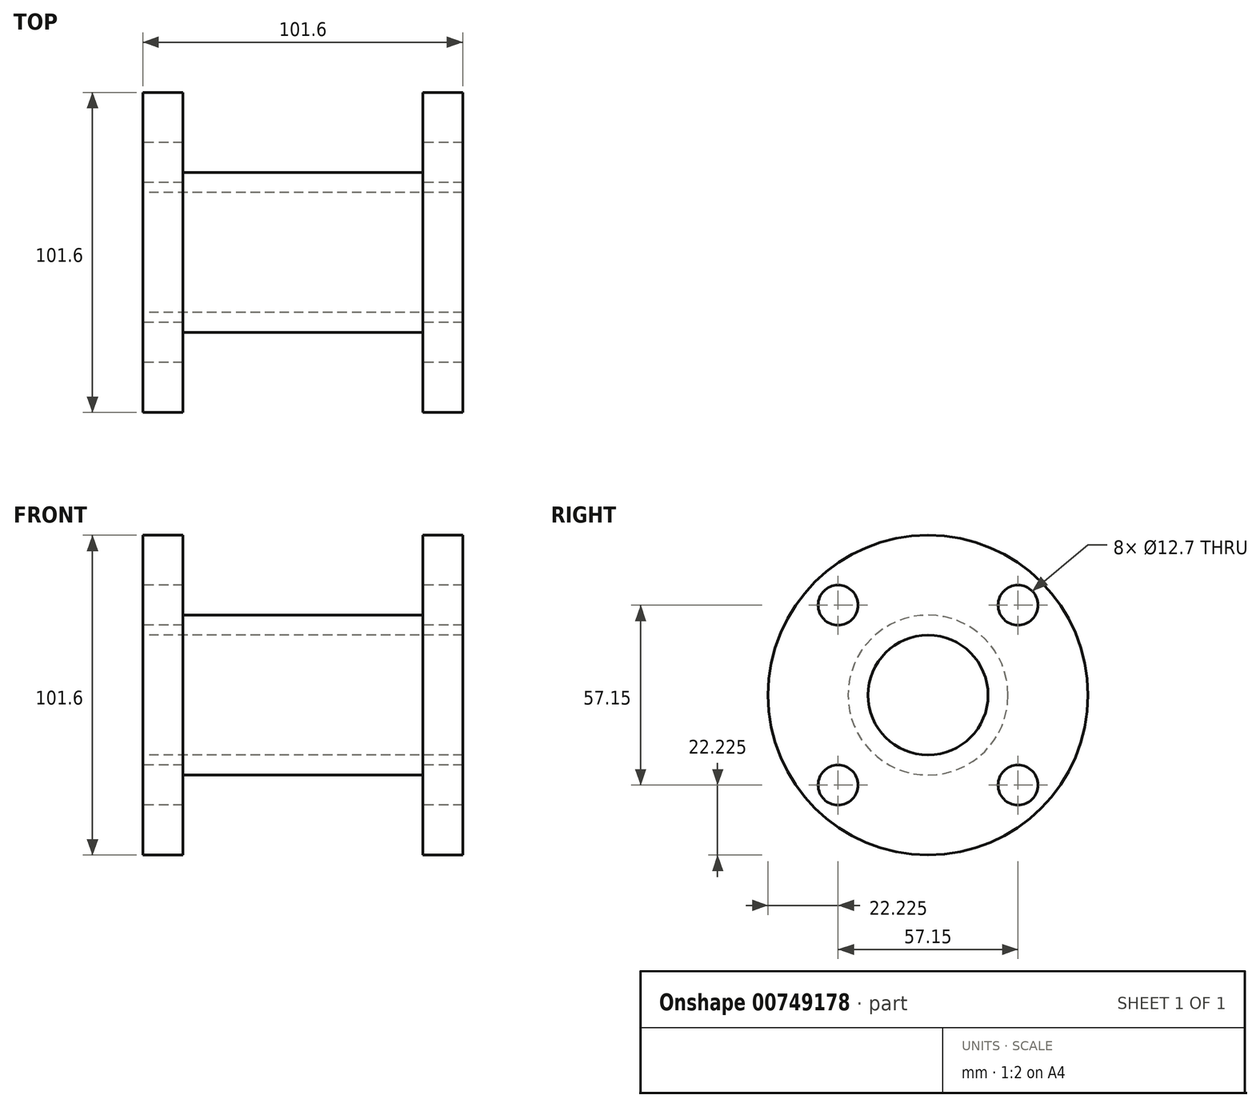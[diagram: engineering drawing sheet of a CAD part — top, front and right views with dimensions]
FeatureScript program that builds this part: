
annotation { "Feature Type Name" : "Feature", "Feature Type Description" : "" }
export const myFeature = defineFeature(function(context is Context, id is Id, definition is map)
    precondition{}
    {
        {
            var Q0;
            Q0=qCreatedBy(makeId("Top.planeOp"),FACE);
            var sketch = newSketch(context, id + "F0", { "sketchPlane" : qUnion([Q0])});
            skLineSegment(sketch, "E0", {"start": v(101.6, -50.8) * mm, "end": v(101.6, -19.05) * mm});
            skLineSegment(sketch, "E1", {"start": v(101.6, -19.05) * mm, "end": v(0, -19.05) * mm});
            skLineSegment(sketch, "E2", {"start": v(0, -19.05) * mm, "end": v(0, -50.8) * mm});
            skLineSegment(sketch, "E3", {"start": v(0, -50.8) * mm, "end": v(101.6, -50.8) * mm});
            skLineSegment(sketch, "E4", {"start": v(0, -25.4) * mm, "end": v(101.6, -25.4) * mm});
            skLineSegment(sketch, "E5", {"start": v(12.7, -19.05) * mm, "end": v(12.7, -50.8) * mm});
            skLineSegment(sketch, "E6", {"start": v(88.9, -19.05) * mm, "end": v(88.9, -50.8) * mm});
            skLineSegment(sketch, "E7", {"start": v(0, 0) * mm, "end": v(101.6, 0) * mm});
            skSolve(sketch);
        }
        {
            var Q0;
            {var subQ0=sQuery(id+"F0.wireOp",EDGE,"E2");var subQ1=sQuery(id+"F0.wireOp",EDGE,"E1");var subQ2=makeQuery(id+"F0.imprint","INTERSECT",VERTEX,{"derivedFrom":[subQ1,subQ0]});Q0=makeQuery(id+"F0.imprint","IMPRINT",FACE,{"disambiguationData":[TD([[makeQuery(id+"F0.imprint","IMPRINT",EDGE,{"disambiguationData":[TD([[subQ2,1.0]])],"derivedFrom":subQ1}),1.0]])]});}
            var Q1;
            {var subQ0=sQuery(id+"F0.wireOp",EDGE,"E3");var subQ1=sQuery(id+"F0.wireOp",EDGE,"E2");var subQ2=makeQuery(id+"F0.imprint","INTERSECT",VERTEX,{"derivedFrom":[subQ1,subQ0]});Q1=makeQuery(id+"F0.imprint","IMPRINT",FACE,{"disambiguationData":[TD([[makeQuery(id+"F0.imprint","IMPRINT",EDGE,{"disambiguationData":[TD([[subQ2,1.0]])],"derivedFrom":subQ1}),1.0]])]});}
            var Q2;
            {var subQ0=sQuery(id+"F0.wireOp",EDGE,"E5");var subQ1=sQuery(id+"F0.wireOp",EDGE,"E1");var subQ2=makeQuery(id+"F0.imprint","INTERSECT",VERTEX,{"derivedFrom":[subQ1,subQ0]});Q2=makeQuery(id+"F0.imprint","IMPRINT",FACE,{"disambiguationData":[TD([[makeQuery(id+"F0.imprint","IMPRINT",EDGE,{"disambiguationData":[TD([[subQ2,1.0]])],"derivedFrom":subQ1}),1.0]])]});}
            var Q3;
            {var subQ0=sQuery(id+"F0.wireOp",EDGE,"E1");var subQ1=sQuery(id+"F0.wireOp",EDGE,"E0");var subQ2=makeQuery(id+"F0.imprint","INTERSECT",VERTEX,{"derivedFrom":[subQ1,subQ0]});Q3=makeQuery(id+"F0.imprint","IMPRINT",FACE,{"disambiguationData":[TD([[makeQuery(id+"F0.imprint","IMPRINT",EDGE,{"disambiguationData":[TD([[subQ2,1.0]])],"derivedFrom":subQ1}),1.0]])]});}
            var Q4;
            {var subQ0=sQuery(id+"F0.wireOp",EDGE,"E3");var subQ1=sQuery(id+"F0.wireOp",EDGE,"E0");var subQ2=makeQuery(id+"F0.imprint","INTERSECT",VERTEX,{"derivedFrom":[subQ1,subQ0]});Q4=makeQuery(id+"F0.imprint","IMPRINT",FACE,{"disambiguationData":[TD([[makeQuery(id+"F0.imprint","IMPRINT",EDGE,{"disambiguationData":[TD([[subQ2,-1.0]])],"derivedFrom":subQ1}),1.0]])]});}
            var Q5;
            Q5=sQuery(id+"F0.wireOp",EDGE,"E7");
            revolve(context, id + "F1", {"surfaceOperationType" : NewSurfaceOperationType.NEW, "entities" : qUnion([Q0, Q1, Q2, Q3, Q4]), "axis" : qUnion([Q5]), "revolveType" : RevolveType.FULL});
        }
        {
            var Q0;
            Q0=makeQuery(id+"F1.opRevolve","SWEPT_FACE",FACE,{"disambiguationData":[OSD([sQuery(id+"F0.wireOp",EDGE,"E2")])]});
            var sketch = newSketch(context, id + "F2", { "sketchPlane" : qUnion([Q0])});
            skCircle(sketch, "E8", {"center": v(-28.58, 28.58) * mm, "radius": 6.35 * mm});
            skCircle(sketch, "E9", {"center": v(28.58, 28.58) * mm, "radius": 6.35 * mm});
            skCircle(sketch, "E10", {"center": v(28.58, -28.58) * mm, "radius": 6.35 * mm});
            skCircle(sketch, "E11", {"center": v(-28.58, -28.58) * mm, "radius": 6.35 * mm});
            skCircle(sketch, "E12.0", {"center": v(0, 0) * mm, "radius": 19.05 * mm});
            skCircle(sketch, "E13.0", {"center": v(0, 0) * mm, "radius": 50.8 * mm});
            skSolve(sketch);
        }
        {
            var Q0;
            Q0=makeQuery(id+"F2.imprint","IMPRINT",FACE,{"disambiguationData":[TD([[makeQuery(id+"F2.imprint","IMPRINT",EDGE,{"derivedFrom":sQuery(id+"F2.wireOp",EDGE,"E8")}),1.0]])]});
            var Q1;
            Q1=makeQuery(id+"F2.imprint","IMPRINT",FACE,{"disambiguationData":[TD([[makeQuery(id+"F2.imprint","IMPRINT",EDGE,{"derivedFrom":sQuery(id+"F2.wireOp",EDGE,"E9")}),1.0]])]});
            var Q2;
            Q2=makeQuery(id+"F2.imprint","IMPRINT",FACE,{"disambiguationData":[TD([[makeQuery(id+"F2.imprint","IMPRINT",EDGE,{"derivedFrom":sQuery(id+"F2.wireOp",EDGE,"E11")}),1.0]])]});
            var Q3;
            Q3=makeQuery(id+"F2.imprint","IMPRINT",FACE,{"disambiguationData":[TD([[makeQuery(id+"F2.imprint","IMPRINT",EDGE,{"derivedFrom":sQuery(id+"F2.wireOp",EDGE,"E10")}),1.0]])]});
            var Q4;
            Q4=makeQuery(id+"F1.opRevolve","SWEPT_FACE",FACE,{"disambiguationData":[OSD([sQuery(id+"F0.wireOp",EDGE,"E0")])]});
            extrude(context, id + "F3", {"entities" : qUnion([Q0, Q1, Q2, Q3]), "operationType" : NewBodyOperationType.REMOVE, "endBound" : BoundingType.UP_TO_SURFACE, "oppositeDirection" : true, "depth" : 25.4 * mm, "endBoundEntityFace" : qUnion([Q4]), "offsetDistance" : 25.4 * mm});
        }
    });
